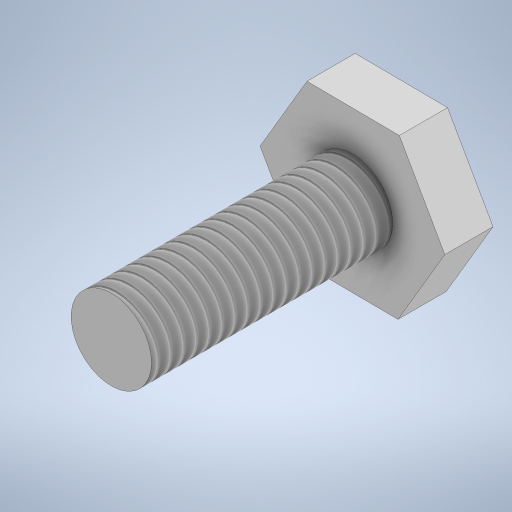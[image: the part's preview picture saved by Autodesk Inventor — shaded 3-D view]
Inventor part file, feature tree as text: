
AUTODESK INVENTOR PART (.ipt)
format: ipt  version: 2024 (Build 280153000, 153)  size: 272,384 bytes
history: native  units: mm
features: sketch x3, extrude x2, thread x1
ambient origin geometry x8: Origin, YZ Plane, XZ Plane, XY Plane, X Axis, Y Axis, Z Axis, Center Point
bodies: Solid1 (feature_tree)
feature tree (6):
  extrude  "Extrusion1"  Depth=10.0mm
  extrude  "Extrusion2"  Depth=15.0mm
  thread  "Thread1"  [1 undecoded]
  sketch  "Sketch3"  dims[d7=15.0mm d8=0.0mm]
  sketch  "Sketch1"  dims[d0=5.0mm d1=10.0mm]
  sketch  "Sketch2"  dims[d2=3.0mm d3=0.0mm d4=5.0mm d5=15.0mm d6=0.0mm]
note: 1 required parameter value undecoded (feature->parameter linkage not recoverable at this tier; creation-order binding heuristic only, values carry confidence <= 0.55)
